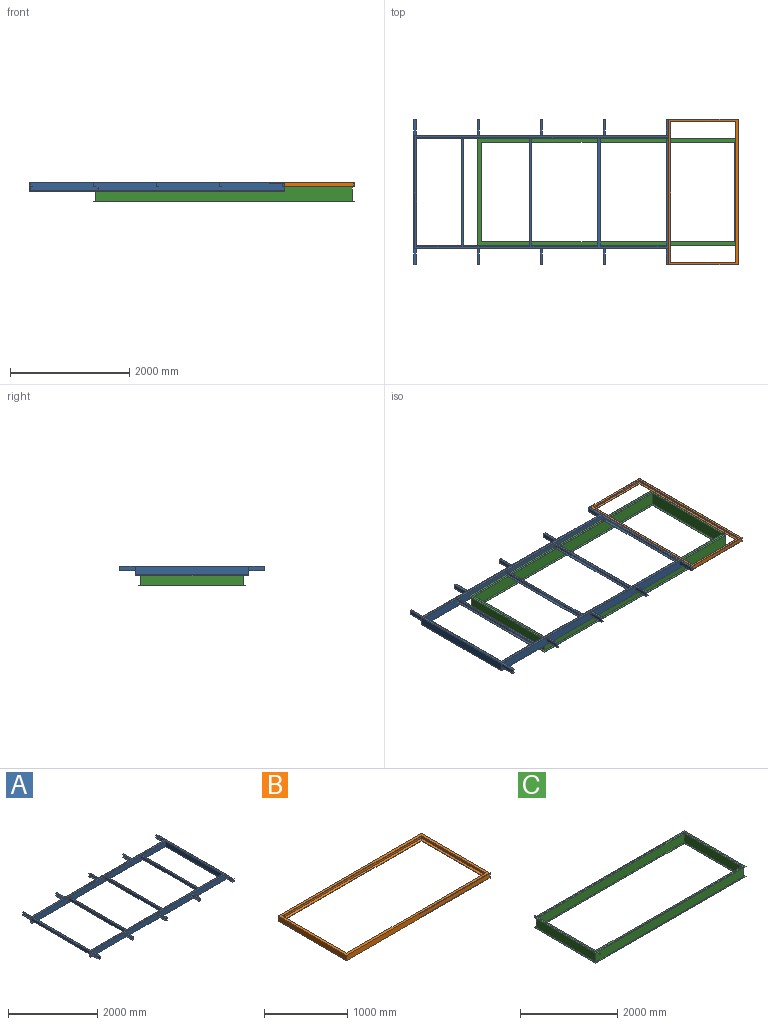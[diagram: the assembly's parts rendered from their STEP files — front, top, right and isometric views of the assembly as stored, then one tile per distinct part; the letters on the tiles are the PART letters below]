
ASSEMBLY  parts=3 mates=2
PART A: 165 faces, bbox 4272.4x2438.4x152.4 mm
  f0: plane 4272.4x142.4mm, normal (0,1,0), area 602302.7mm2, adj f17,f19,f20,f25,f115,f116,f121,f122
  f1: plane 66.04x31.75mm, normal (0,1,0), area 1940.6mm2, adj f17,f117,f118,f119
  f2: plane 4272.4x142.4mm, normal (0,-1,0), area 602302.7mm2, adj f17,f25,f30,f31,f69,f70,f73,f75
  f3: plane 66.04x31.75mm, normal (0,-1,0), area 1940.6mm2, adj f17,f66,f67,f68
  f4: plane 4221.6x142.4mm, normal (0,-1,0), area 597781.5mm2, adj f6,f7,f8,f17,f18,f21,f22,f35
  f5: plane 4221.6x142.4mm, normal (0,1,0), area 597781.5mm2, adj f17,f22,f28,f33,f35,f36,f37,f38
  f6: cylinder r=5mm len=754.73mm, axis (-1,0,0), area 5902.7mm2, adj f4,f27,f32,f62
  f7: cylinder r=5mm len=1106.49mm, axis (-1,0,0), area 8690.3mm2, adj f4,f32,f54,f63
  f8: cylinder r=5mm len=1106.49mm, axis (-1,0,0), area 8690.3mm2, adj f4,f32,f46,f55
  f9: plane 4231.12x133.35mm, normal (0,1,0), area 563934.9mm2, adj f12,f14,f16,f17,f164
  f10: plane 4262.87x133.35mm, normal (0,-1,0), area 568168.8mm2, adj f11,f14,f16,f17,f163
  f11: plane 1885.95x133.35mm, normal (-1,0,0), area 251491.4mm2, adj f10,f13,f14,f16
  f12: plane 1822.45x133.35mm, normal (1,0,0), area 243023.7mm2, adj f9,f14,f15,f16
  f13: plane 4262.87x133.35mm, normal (0,1,0), area 568168.8mm2, adj f11,f14,f16,f17,f162
  f14: plane 4262.87x1885.95mm, normal (0,0,1), area 328555.1mm2, adj f9,f10,f11,f12,f13,f15,f17
  f15: plane 4231.12x133.35mm, normal (0,-1,0), area 563934.9mm2, adj f12,f14,f16,f17,f161
  f16: plane 4262.87x1885.95mm, normal (0,0,-1), area 328555.1mm2, adj f9,f10,f11,f12,f13,f15,f17
  f17: plane 2438.4x152.4mm, normal (-1,0,0), area 149817mm2, adj f0,f1,f2,f3,f4,f5,f9,f10
  f18: cylinder r=5mm len=1106.49mm, axis (-1,0,0), area 8690.3mm2, adj f4,f32,f39,f47
  f19: cylinder r=5mm len=4272.4mm, axis (-1,0,0), area 33541mm2, adj f0,f17,f26,f32,f113,f130,f140,f150
  f20: cylinder r=5mm len=4272.4mm, axis (-1,0,0), area 33541mm2, adj f0,f17,f24,f29
  f21: cylinder r=5mm len=4226.6mm, axis (-1,0,0), area 33170.6mm2, adj f4,f17,f23,f29
  f22: plane 1803.4x142.4mm, normal (-1,0,0), area 256804.2mm2, adj f4,f5,f23,f27
  f23: cylinder r=5mm len=1813.4mm, axis (0,1,0), area 14192.4mm2, adj f21,f22,f28,f29
  f24: cylinder r=5mm len=1905mm, axis (0,1,0), area 14933.3mm2, adj f20,f25,f29,f30
  f25: plane 1905x142.4mm, normal (1,0,0), area 271272mm2, adj f0,f2,f24,f26
  f26: cylinder r=5mm len=1905mm, axis (0,1,0), area 14933.3mm2, adj f19,f25,f31,f32
  f27: cylinder r=5mm len=1813.4mm, axis (0,1,0), area 14192.4mm2, adj f6,f22,f32,f33
  f28: cylinder r=5mm len=4226.6mm, axis (1,0,0), area 33170.6mm2, adj f5,f17,f23,f29
  f29: plane 4267.4x1895mm, normal (0,0,-1), area 422206.2mm2, adj f17,f20,f21,f23,f24,f28,f30
  f30: cylinder r=5mm len=4272.4mm, axis (1,0,0), area 33541mm2, adj f2,f17,f24,f29
  f31: cylinder r=5mm len=4272.4mm, axis (1,0,0), area 33541mm2, adj f2,f17,f26,f32,f65,f82,f92,f102
  f32: plane 4267.4x1895mm, normal (0,0,1), area 697806.3mm2, adj f6,f7,f8,f17,f18,f19,f26,f27
  f33: cylinder r=5mm len=4226.6mm, axis (1,0,0), area 33170.6mm2, adj f5,f17,f27,f32,f34,f41,f49,f57
  f34: plane 38.1x5mm, normal (0,-1,0), area 190.5mm2, adj f17,f32,f33,f39
  f35: plane 1803.4x5.08mm, normal (1,0,0), area 9161.3mm2, adj f4,f5,f36,f38
  f36: plane 1803.4x31.75mm, normal (0.15,0,0.99), area 57941.3mm2, adj f4,f5,f35,f37
  f37: plane 1803.4x56.2mm, normal (1,0,0), area 101351.1mm2, adj f4,f5,f36,f40
  f38: plane 1803.4x38.1mm, normal (0,0,-1), area 68709.5mm2, adj f4,f5,f17,f35
  f39: plane 1808.4x5.08mm, normal (1,0,0), area 9166.6mm2, adj f4,f5,f18,f32,f34,f40
  f40: plane 1803.4x31.75mm, normal (0.15,0,-0.99), area 57941.3mm2, adj f4,f5,f37,f39
  f41: plane 38.1x5mm, normal (0,-1,0), area 190.5mm2, adj f32,f33,f46,f47
  f42: plane 1803.4x38.1mm, normal (0,0,-1), area 68709.5mm2, adj f4,f5,f43,f47
  f43: plane 1803.4x5.08mm, normal (1,0,0), area 9161.3mm2, adj f4,f5,f42,f44
  f44: plane 1803.4x31.75mm, normal (0.15,0,0.99), area 57941.3mm2, adj f4,f5,f43,f45
  f45: plane 1803.4x56.2mm, normal (1,0,0), area 101351.1mm2, adj f4,f5,f44,f48
  f46: plane 1808.4x5.08mm, normal (1,0,0), area 9166.6mm2, adj f4,f5,f8,f32,f41,f48
  f47: plane 1808.4x76.2mm, normal (-1,0,0), area 137424.4mm2, adj f4,f5,f18,f32,f41,f42
  f48: plane 1803.4x31.75mm, normal (0.15,0,-0.99), area 57941.3mm2, adj f4,f5,f45,f46
  f49: plane 38.1x5mm, normal (0,-1,0), area 190.5mm2, adj f32,f33,f54,f55
  f50: plane 1803.4x38.1mm, normal (0,0,-1), area 68709.5mm2, adj f4,f5,f51,f55
  f51: plane 1803.4x5.08mm, normal (1,0,0), area 9161.3mm2, adj f4,f5,f50,f52
  f52: plane 1803.4x31.75mm, normal (0.15,0,0.99), area 57941.3mm2, adj f4,f5,f51,f53
  f53: plane 1803.4x56.2mm, normal (1,0,0), area 101351.1mm2, adj f4,f5,f52,f56
  f54: plane 1808.4x5.08mm, normal (1,0,0), area 9166.6mm2, adj f4,f5,f7,f32,f49,f56
  f55: plane 1808.4x76.2mm, normal (-1,0,0), area 137424.4mm2, adj f4,f5,f8,f32,f49,f50
  f56: plane 1803.4x31.75mm, normal (0.15,0,-0.99), area 57941.3mm2, adj f4,f5,f53,f54
  f57: plane 38.1x5mm, normal (0,-1,0), area 190.5mm2, adj f32,f33,f62,f63
  f58: plane 1803.4x38.1mm, normal (0,0,-1), area 68709.5mm2, adj f4,f5,f59,f63
  f59: plane 1803.4x5.08mm, normal (1,0,0), area 9161.3mm2, adj f4,f5,f58,f60
  f60: plane 1803.4x31.75mm, normal (0.15,0,0.99), area 57941.3mm2, adj f4,f5,f59,f61
  f61: plane 1803.4x56.2mm, normal (1,0,0), area 101351.1mm2, adj f4,f5,f60,f64
  f62: plane 1808.4x5.08mm, normal (1,0,0), area 9166.6mm2, adj f4,f5,f6,f32,f57,f64
  f63: plane 1808.4x76.2mm, normal (-1,0,0), area 137424.4mm2, adj f4,f5,f7,f32,f57,f58
  f64: plane 1803.4x31.75mm, normal (0.15,0,-0.99), area 57941.3mm2, adj f4,f5,f61,f62
  f65: plane 38.1x5mm, normal (0,1,0), area 190.5mm2, adj f17,f31,f70,f71
  f66: plane 266.7x31.75mm, normal (-0.15,0,-0.99), area 8568.8mm2, adj f3,f17,f67,f72
  f67: plane 266.7x56.2mm, normal (-1,0,0), area 14988.5mm2, adj f3,f66,f68,f72
  f68: plane 266.7x31.75mm, normal (-0.15,0,0.99), area 8568.8mm2, adj f3,f17,f67,f72
  f69: plane 266.7x38.1mm, normal (0,0,-1), area 10161.3mm2, adj f2,f17,f70,f72
  f70: plane 266.7x76.2mm, normal (1,0,0), area 20322.5mm2, adj f2,f65,f69,f71,f72
  f71: plane 266.7x38.1mm, normal (0,0,1), area 10161.3mm2, adj f17,f65,f70,f72
  f72: plane 76.2x38.1mm, normal (0,-1,0), area 962.7mm2, adj f17,f66,f67,f68,f69,f70,f71
  f73: plane 266.7x76.2mm, normal (1,0,0), area 20322.5mm2, adj f2,f74,f80,f81,f82
  f74: plane 266.7x38.1mm, normal (0,0,1), area 10161.3mm2, adj f73,f75,f81,f82
  f75: plane 266.7x5.08mm, normal (-1,0,0), area 1354.8mm2, adj f2,f74,f76,f81,f82
  f76: plane 266.7x31.75mm, normal (-0.15,0,-0.99), area 8568.8mm2, adj f2,f75,f77,f81
  f77: plane 266.7x56.2mm, normal (-1,0,0), area 14988.5mm2, adj f2,f76,f78,f81
  f78: plane 266.7x31.75mm, normal (-0.15,0,0.99), area 8568.8mm2, adj f2,f77,f79,f81
  f79: plane 266.7x5.08mm, normal (-1,0,0), area 1354.8mm2, adj f2,f78,f80,f81
  f80: plane 266.7x38.1mm, normal (0,0,-1), area 10161.3mm2, adj f2,f73,f79,f81
  f81: plane 76.2x38.1mm, normal (0,-1,0), area 962.7mm2, adj f73,f74,f75,f76,f77,f78,f79,f80
  f82: plane 38.1x5mm, normal (0,1,0), area 190.5mm2, adj f31,f73,f74,f75
  f83: plane 266.7x76.2mm, normal (1,0,0), area 20322.5mm2, adj f2,f84,f90,f91,f92
  f84: plane 266.7x38.1mm, normal (0,0,1), area 10161.3mm2, adj f83,f85,f91,f92
  f85: plane 266.7x5.08mm, normal (-1,0,0), area 1354.8mm2, adj f2,f84,f86,f91,f92
  f86: plane 266.7x31.75mm, normal (-0.15,0,-0.99), area 8568.8mm2, adj f2,f85,f87,f91
  f87: plane 266.7x56.2mm, normal (-1,0,0), area 14988.5mm2, adj f2,f86,f88,f91
  f88: plane 266.7x31.75mm, normal (-0.15,0,0.99), area 8568.8mm2, adj f2,f87,f89,f91
  f89: plane 266.7x5.08mm, normal (-1,0,0), area 1354.8mm2, adj f2,f88,f90,f91
  f90: plane 266.7x38.1mm, normal (0,0,-1), area 10161.3mm2, adj f2,f83,f89,f91
  f91: plane 76.2x38.1mm, normal (0,-1,0), area 962.7mm2, adj f83,f84,f85,f86,f87,f88,f89,f90
  f92: plane 38.1x5mm, normal (0,1,0), area 190.5mm2, adj f31,f83,f84,f85
  f93: plane 266.7x76.2mm, normal (1,0,0), area 20322.5mm2, adj f2,f94,f100,f101,f102
  f94: plane 266.7x38.1mm, normal (0,0,1), area 10161.3mm2, adj f93,f95,f101,f102
  f95: plane 266.7x5.08mm, normal (-1,0,0), area 1354.8mm2, adj f2,f94,f96,f101,f102
  f96: plane 266.7x31.75mm, normal (-0.15,0,-0.99), area 8568.8mm2, adj f2,f95,f97,f101
  f97: plane 266.7x56.2mm, normal (-1,0,0), area 14988.5mm2, adj f2,f96,f98,f101
  f98: plane 266.7x31.75mm, normal (-0.15,0,0.99), area 8568.8mm2, adj f2,f97,f99,f101
  f99: plane 266.7x5.08mm, normal (-1,0,0), area 1354.8mm2, adj f2,f98,f100,f101
  f100: plane 266.7x38.1mm, normal (0,0,-1), area 10161.3mm2, adj f2,f93,f99,f101
  f101: plane 76.2x38.1mm, normal (0,-1,0), area 962.7mm2, adj f93,f94,f95,f96,f97,f98,f99,f100
  f102: plane 38.1x5mm, normal (0,1,0), area 190.5mm2, adj f31,f93,f94,f95
  f103: plane 266.7x38.1mm, normal (0,0,1), area 10161.3mm2, adj f104,f110,f111,f112
  f104: plane 266.7x5.08mm, normal (-1,0,0), area 1354.8mm2, adj f2,f103,f105,f111,f112
  f105: plane 266.7x31.75mm, normal (-0.15,0,-0.99), area 8568.8mm2, adj f2,f104,f106,f111
  f106: plane 266.7x56.2mm, normal (-1,0,0), area 14988.5mm2, adj f2,f105,f107,f111
  f107: plane 266.7x31.75mm, normal (-0.15,0,0.99), area 8568.8mm2, adj f2,f106,f108,f111
  f108: plane 266.7x5.08mm, normal (-1,0,0), area 1354.8mm2, adj f2,f107,f109,f111
  f109: plane 266.7x38.1mm, normal (0,0,-1), area 10161.3mm2, adj f2,f108,f110,f111
  f110: plane 266.7x76.2mm, normal (1,0,0), area 20322.5mm2, adj f2,f103,f109,f111,f112
  f111: plane 76.2x38.1mm, normal (0,-1,0), area 962.7mm2, adj f103,f104,f105,f106,f107,f108,f109,f110
  f112: plane 38.1x5mm, normal (0,1,0), area 190.5mm2, adj f31,f103,f104,f110
  f113: plane 38.1x5mm, normal (0,-1,0), area 190.5mm2, adj f17,f19,f114,f115
  f114: plane 266.7x38.1mm, normal (0,0,1), area 10161.3mm2, adj f17,f113,f115,f120
  f115: plane 266.7x76.2mm, normal (1,0,0), area 20322.5mm2, adj f0,f113,f114,f116,f120
  f116: plane 266.7x38.1mm, normal (0,0,-1), area 10161.3mm2, adj f0,f17,f115,f120
  f117: plane 266.7x31.75mm, normal (-0.15,0,0.99), area 8568.8mm2, adj f1,f17,f118,f120
  f118: plane 266.7x56.2mm, normal (-1,0,0), area 14988.5mm2, adj f1,f117,f119,f120
  f119: plane 266.7x31.75mm, normal (-0.15,0,-0.99), area 8568.8mm2, adj f1,f17,f118,f120
  f120: plane 76.2x38.1mm, normal (0,1,0), area 962.7mm2, adj f17,f114,f115,f116,f117,f118,f119
  f121: plane 266.7x76.2mm, normal (1,0,0), area 20322.5mm2, adj f0,f122,f128,f129,f130
  f122: plane 266.7x38.1mm, normal (0,0,-1), area 10161.3mm2, adj f0,f121,f123,f129
  f123: plane 266.7x5.08mm, normal (-1,0,0), area 1354.8mm2, adj f0,f122,f124,f129
  f124: plane 266.7x31.75mm, normal (-0.15,0,0.99), area 8568.8mm2, adj f0,f123,f125,f129
  f125: plane 266.7x56.2mm, normal (-1,0,0), area 14988.5mm2, adj f0,f124,f126,f129
  f126: plane 266.7x31.75mm, normal (-0.15,0,-0.99), area 8568.8mm2, adj f0,f125,f127,f129
  f127: plane 266.7x5.08mm, normal (-1,0,0), area 1354.8mm2, adj f0,f126,f128,f129,f130
  f128: plane 266.7x38.1mm, normal (0,0,1), area 10161.3mm2, adj f121,f127,f129,f130
  f129: plane 76.2x38.1mm, normal (0,1,0), area 962.7mm2, adj f121,f122,f123,f124,f125,f126,f127,f128
  f130: plane 38.1x5mm, normal (0,-1,0), area 190.5mm2, adj f19,f121,f127,f128
  f131: plane 266.7x5.08mm, normal (-1,0,0), area 1354.8mm2, adj f0,f132,f138,f139,f140
  f132: plane 266.7x38.1mm, normal (0,0,1), area 10161.3mm2, adj f131,f133,f139,f140
  f133: plane 266.7x76.2mm, normal (1,0,0), area 20322.5mm2, adj f0,f132,f134,f139,f140
  f134: plane 266.7x38.1mm, normal (0,0,-1), area 10161.3mm2, adj f0,f133,f135,f139
  f135: plane 266.7x5.08mm, normal (-1,0,0), area 1354.8mm2, adj f0,f134,f136,f139
  f136: plane 266.7x31.75mm, normal (-0.15,0,0.99), area 8568.8mm2, adj f0,f135,f137,f139
  f137: plane 266.7x56.2mm, normal (-1,0,0), area 14988.5mm2, adj f0,f136,f138,f139
  f138: plane 266.7x31.75mm, normal (-0.15,0,-0.99), area 8568.8mm2, adj f0,f131,f137,f139
  f139: plane 76.2x38.1mm, normal (0,1,0), area 962.7mm2, adj f131,f132,f133,f134,f135,f136,f137,f138
  f140: plane 38.1x5mm, normal (0,-1,0), area 190.5mm2, adj f19,f131,f132,f133
  f141: plane 266.7x76.2mm, normal (1,0,0), area 20322.5mm2, adj f0,f142,f148,f149,f150
  f142: plane 266.7x38.1mm, normal (0,0,-1), area 10161.3mm2, adj f0,f141,f143,f149
  f143: plane 266.7x5.08mm, normal (-1,0,0), area 1354.8mm2, adj f0,f142,f144,f149
  f144: plane 266.7x31.75mm, normal (-0.15,0,0.99), area 8568.8mm2, adj f0,f143,f145,f149
  f145: plane 266.7x56.2mm, normal (-1,0,0), area 14988.5mm2, adj f0,f144,f146,f149
  f146: plane 266.7x31.75mm, normal (-0.15,0,-0.99), area 8568.8mm2, adj f0,f145,f147,f149
  f147: plane 266.7x5.08mm, normal (-1,0,0), area 1354.8mm2, adj f0,f146,f148,f149,f150
  f148: plane 266.7x38.1mm, normal (0,0,1), area 10161.3mm2, adj f141,f147,f149,f150
  f149: plane 76.2x38.1mm, normal (0,1,0), area 962.7mm2, adj f141,f142,f143,f144,f145,f146,f147,f148
  f150: plane 38.1x5mm, normal (0,-1,0), area 190.5mm2, adj f19,f141,f147,f148
  f151: plane 266.7x76.2mm, normal (1,0,0), area 20322.5mm2, adj f0,f152,f158,f159,f160
  f152: plane 266.7x38.1mm, normal (0,0,-1), area 10161.3mm2, adj f0,f151,f153,f159
  f153: plane 266.7x5.08mm, normal (-1,0,0), area 1354.8mm2, adj f0,f152,f154,f159
  f154: plane 266.7x31.75mm, normal (-0.15,0,0.99), area 8568.8mm2, adj f0,f153,f155,f159
  f155: plane 266.7x56.2mm, normal (-1,0,0), area 14988.5mm2, adj f0,f154,f156,f159
  f156: plane 266.7x31.75mm, normal (-0.15,0,-0.99), area 8568.8mm2, adj f0,f155,f157,f159
  f157: plane 266.7x5.08mm, normal (-1,0,0), area 1354.8mm2, adj f0,f156,f158,f159,f160
  f158: plane 266.7x38.1mm, normal (0,0,1), area 10161.3mm2, adj f151,f157,f159,f160
  f159: plane 76.2x38.1mm, normal (0,1,0), area 962.7mm2, adj f151,f152,f153,f154,f155,f156,f157,f158
  f160: plane 38.1x5mm, normal (0,-1,0), area 190.5mm2, adj f19,f151,f157,f158
  f161: cylinder r=9.53mm len=19.05mm, axis (0,1,0), area 570mm2, adj f5,f15
  f162: cylinder r=9.53mm len=19.05mm, axis (0,1,0), area 570mm2, adj f2,f13
  f163: cylinder r=9.53mm len=19.05mm, axis (0,1,0), area 570mm2, adj f0,f10
  f164: cylinder r=9.53mm len=19.05mm, axis (0,1,0), area 570mm2, adj f4,f9
PART B: 26 faces, bbox 2438.4x1170x76.2 mm
  f0: plane 2438.4x76.2mm, normal (0,1,0), area 185806.1mm2, adj f6,f12,f23,f24
  f1: plane 2425.7x31.75mm, normal (0,-0.15,0.99), area 76915.1mm2, adj f2,f5,f7,f13
  f2: plane 2425.7x56.2mm, normal (0,-1,0), area 136324.3mm2, adj f1,f3,f8,f14
  f3: plane 2425.7x31.75mm, normal (0,-0.15,-0.99), area 76915.1mm2, adj f2,f4,f9,f15
  f4: plane 2362.2x5.08mm, normal (0,-1,0), area 12000mm2, adj f3,f10,f16,f23
  f5: plane 2362.2x5.08mm, normal (0,-1,0), area 12000mm2, adj f1,f11,f17,f24
  f6: plane 1170x76.2mm, normal (-1,0,0), area 89154mm2, adj f0,f18,f23,f24
  f7: plane 1157.3x31.75mm, normal (0.15,0,0.99), area 36162.7mm2, adj f1,f8,f11,f19
  f8: plane 1157.3x56.2mm, normal (1,0,0), area 65040.3mm2, adj f2,f7,f9,f20
  f9: plane 1157.3x31.75mm, normal (0.15,0,-0.99), area 36162.7mm2, adj f3,f8,f10,f21
  f10: plane 1093.8x5.08mm, normal (1,0,0), area 5556.5mm2, adj f4,f9,f22,f23
  f11: plane 1093.8x5.08mm, normal (1,0,0), area 5556.5mm2, adj f5,f7,f24,f25
  f12: plane 1170x76.2mm, normal (1,0,0), area 89154mm2, adj f0,f18,f23,f24
  f13: plane 1157.3x31.75mm, normal (-0.15,0,0.99), area 36162.7mm2, adj f1,f14,f17,f19
  f14: plane 1157.3x56.2mm, normal (-1,0,0), area 65040.3mm2, adj f2,f13,f15,f20
  f15: plane 1157.3x31.75mm, normal (-0.15,0,-0.99), area 36162.7mm2, adj f3,f14,f16,f21
  f16: plane 1093.8x5.08mm, normal (-1,0,0), area 5556.5mm2, adj f4,f15,f22,f23
  f17: plane 1093.8x5.08mm, normal (-1,0,0), area 5556.5mm2, adj f5,f13,f24,f25
  f18: plane 2438.4x76.2mm, normal (0,-1,0), area 185806.1mm2, adj f6,f12,f23,f24
  f19: plane 2425.7x31.75mm, normal (0,0.15,0.99), area 76915.1mm2, adj f7,f13,f20,f25
  f20: plane 2425.7x56.2mm, normal (0,1,0), area 136324.3mm2, adj f8,f14,f19,f21
  f21: plane 2425.7x31.75mm, normal (0,0.15,-0.99), area 76915.1mm2, adj f9,f15,f20,f22
  f22: plane 2362.2x5.08mm, normal (0,1,0), area 12000mm2, adj f10,f16,f21,f23
  f23: plane 2438.4x1170mm, normal (0,0,1), area 269153.6mm2, adj f0,f4,f6,f10,f12,f16,f18,f22
  f24: plane 2438.4x1170mm, normal (0,0,-1), area 269153.6mm2, adj f0,f5,f6,f11,f12,f17,f18,f25
  f25: plane 2362.2x5.08mm, normal (0,1,0), area 12000mm2, adj f11,f17,f19,f24
PART C: 34 faces, bbox 4368.8x1905x254 mm
  f0: plane 4368.8x3.18mm, normal (0,1,0), area 13870.9mm2, adj f6,f12,f20,f21
  f1: plane 4368.8x3.18mm, normal (0,1,0), area 13870.9mm2, adj f7,f13,f23,f24
  f2: plane 4305.3x247.65mm, normal (0,1,0), area 1065922.5mm2, adj f8,f14,f21,f23,f32
  f3: plane 4235.45x3.18mm, normal (0,-1,0), area 13447.6mm2, adj f9,f15,f24,f26
  f4: plane 4298.95x247.65mm, normal (0,-1,0), area 1064635mm2, adj f10,f16,f26,f28
  f5: plane 4235.45x3.18mm, normal (0,-1,0), area 13447.6mm2, adj f11,f17,f20,f28
  f6: plane 1803.4x3.18mm, normal (-1,0,0), area 5725.8mm2, adj f0,f18,f20,f21
  f7: plane 1803.4x3.18mm, normal (-1,0,0), area 5725.8mm2, adj f1,f19,f23,f24
  f8: plane 1739.9x247.65mm, normal (-1,0,0), area 430886.2mm2, adj f2,f21,f22,f23
  f9: plane 1670.05x3.18mm, normal (1,0,0), area 5302.4mm2, adj f3,f24,f25,f26
  f10: plane 1733.55x247.65mm, normal (1,0,0), area 429313.7mm2, adj f4,f26,f27,f28
  f11: plane 1670.05x3.18mm, normal (1,0,0), area 5302.4mm2, adj f5,f20,f28,f29
  f12: plane 1803.4x3.18mm, normal (1,0,0), area 5725.8mm2, adj f0,f18,f20,f21
  f13: plane 1803.4x3.18mm, normal (1,0,0), area 5725.8mm2, adj f1,f19,f23,f24
  f14: plane 1739.9x247.65mm, normal (1,0,0), area 430886.2mm2, adj f2,f21,f22,f23
  f15: plane 1670.05x3.18mm, normal (-1,0,0), area 5302.4mm2, adj f3,f24,f25,f26
  f16: plane 1733.55x247.65mm, normal (-1,0,0), area 429313.7mm2, adj f4,f26,f27,f28
  f17: plane 1670.05x3.18mm, normal (-1,0,0), area 5302.4mm2, adj f5,f20,f28,f29
  f18: plane 4368.8x3.18mm, normal (0,-1,0), area 13870.9mm2, adj f6,f12,f20,f21
  f19: plane 4368.8x3.18mm, normal (0,-1,0), area 13870.9mm2, adj f7,f13,f23,f24
  f20: plane 4368.8x1803.4mm, normal (0,0,1), area 805280.6mm2, adj f0,f5,f6,f11,f12,f17,f18,f29
  f21: plane 4368.8x1803.4mm, normal (0,0,-1), area 387902.4mm2, adj f0,f2,f6,f8,f12,f14,f18,f22
  f22: plane 4305.3x247.65mm, normal (0,-1,0), area 1065922.5mm2, adj f8,f14,f21,f23,f30
  f23: plane 4368.8x1803.4mm, normal (0,0,1), area 387902.5mm2, adj f1,f2,f7,f8,f13,f14,f19,f22
  f24: plane 4368.8x1803.4mm, normal (0,0,-1), area 805280.6mm2, adj f1,f3,f7,f9,f13,f15,f19,f25
  f25: plane 4235.45x3.18mm, normal (0,1,0), area 13447.6mm2, adj f9,f15,f24,f26
  f26: plane 4298.95x1733.55mm, normal (0,0,1), area 379031.5mm2, adj f3,f4,f9,f10,f15,f16,f25,f27
  f27: plane 4298.95x247.65mm, normal (0,1,0), area 1064635mm2, adj f10,f16,f26,f28
  f28: plane 4298.95x1733.55mm, normal (0,0,-1), area 379031.5mm2, adj f4,f5,f10,f11,f16,f17,f27,f29
  f29: plane 4235.45x3.18mm, normal (0,1,0), area 13447.6mm2, adj f11,f17,f20,f28
  f30: cylinder r=9.53mm len=82.55mm, axis (0,1,0), area 4940.4mm2, adj f22,f31
  f31: plane 19.05x19.05mm, normal (0,-1,0), area 285mm2, adj f30
  f32: cylinder r=9.53mm len=82.55mm, axis (0,-1,0), area 4940.4mm2, adj f2,f33
  f33: plane 19.05x19.05mm, normal (0,1,0), area 285mm2, adj f32
PLACE A rot(axis=(0,0,-1),180deg) t=(-1171.75,901.64,323.33)mm
PLACE B rot(axis=(0,0,1),90deg) t=(-0.13,-1219.26,327.33)mm
PLACE C t=(-4368.93,-901.76,251.13)mm fixed
MATE revolute A.f161 <-> C.f32  axis (0,-1,0) through (-4293.93,-952.56,221.13)mm
MATE fastened B.f24 <-> C.f20  axis (0,0,-1) through (-0.13,-0.06,251.13)mm
